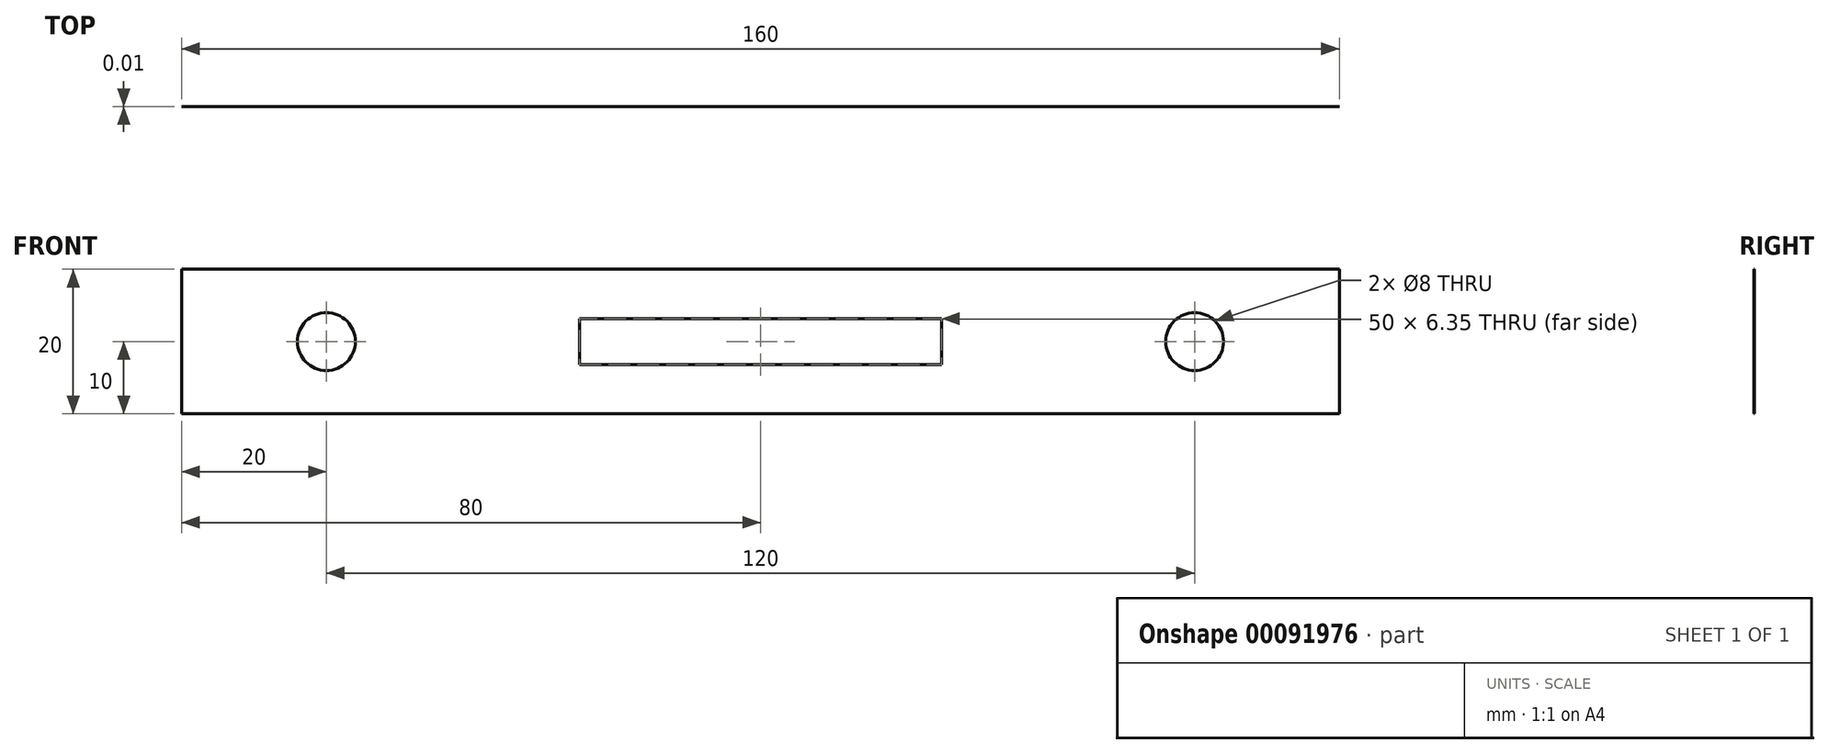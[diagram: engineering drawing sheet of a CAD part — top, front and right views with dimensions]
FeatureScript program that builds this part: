
annotation { "Feature Type Name" : "Feature", "Feature Type Description" : "" }
export const myFeature = defineFeature(function(context is Context, id is Id, definition is map)
    precondition{}
    {
        {
            var Q0;
            Q0=qCreatedBy(makeId("Front.planeOp"),FACE);
            var sketch = newSketch(context, id + "F0", { "sketchPlane" : qUnion([Q0])});
            skLineSegment(sketch, "E0.bottom", {"start": v(80, -10) * mm, "end": v(-80, -10) * mm});
            skLineSegment(sketch, "E0.top", {"start": v(80, 10) * mm, "end": v(-80, 10) * mm});
            skLineSegment(sketch, "E0.left", {"start": v(80, -10) * mm, "end": v(80, 10) * mm});
            skLineSegment(sketch, "E0.right", {"start": v(-80, -10) * mm, "end": v(-80, 10) * mm});
            skPoint(sketch, "E0.middle", {"position": v(0, 0) * mm});
            skLineSegment(sketch, "E1", {"start": v(0, 0) * mm, "end": v(-60, 0) * mm, "construction": true});
            skCircle(sketch, "E2", {"center": v(-60, 0) * mm, "radius": 4 * mm});
            skCircle(sketch, "E3.MirrorC", {"center": v(60, 0) * mm, "radius": 4 * mm});
            skLineSegment(sketch, "E4.bottom", {"start": v(25, 3.18) * mm, "end": v(-25, 3.17) * mm});
            skLineSegment(sketch, "E4.top", {"start": v(25, -3.17) * mm, "end": v(-25, -3.18) * mm});
            skLineSegment(sketch, "E4.left", {"start": v(25, 3.18) * mm, "end": v(25, -3.17) * mm});
            skLineSegment(sketch, "E4.right", {"start": v(-25, 3.17) * mm, "end": v(-25, -3.18) * mm});
            skSolve(sketch);
        }
        {
            var Q0;
            Q0=makeQuery(id+"F0.imprint","IMPRINT",FACE,{"disambiguationData":[TD([[makeQuery(id+"F0.imprint","IMPRINT",EDGE,{"derivedFrom":sQuery(id+"F0.wireOp",EDGE,"E0.bottom")}),-1.0]])]});
            extrude(context, id + "F1", {"entities" : qUnion([Q0]), "depth" : 1 / 101.6 * mm});
        }
    });
